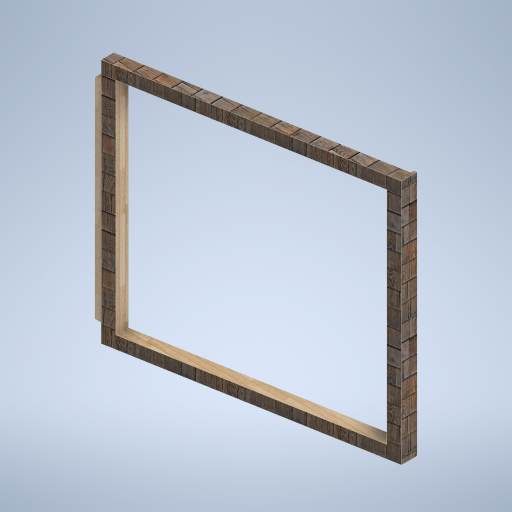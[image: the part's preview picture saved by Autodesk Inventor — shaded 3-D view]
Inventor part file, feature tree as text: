
AUTODESK INVENTOR PART (.ipt)
format: ipt  version: 2024.2 (Build 282272000, 272)  size: 413,184 bytes
history: native  units: mm
features: sketch x9, plane x4, extrude x4, loft x1, other x1, projected_geometry x1
ambient origin geometry x8: Origin, YZ Plane, XZ Plane, XY Plane, X Axis, Y Axis, Z Axis, Center Point
bodies: Solid1 (feature_tree)
feature tree (20):
  sketch  "Sketch1"  dims[d0=0.0mm d1=2500.0mm d2=150.0mm]
  plane  "Work Plane2"
  extrude  "Extrusion1"  Depth=150.0mm
  sketch  "Sketch2"  dims[d3=60.0mm d4=0.0mm d5=0.0mm]
  plane  "Work Plane3"
  sketch  "Sketch3"  dims[d6=13.962634mm d7=13.962634mm]
  plane  "Work Plane4"
  sketch  "Sketch4"  dims[d8=0.0mm d9=90.0deg d10=0.0mm d11=90.0deg]
  loft  "Loft1"
  extrude  "Extrusion2"  Depth=13.962634mm
  extrude  "Extrusion3"  TaperAngle=0.0deg  [1 undecoded]
  sketch  "Sketch8"  dims[d18=0.0mm d19=0.0mm]
  extrude  "Extrusion4"  Depth=2450.0mm
  plane  "Work Plane1"
  sketch  "Sketch5"  dims[d12=0.0mm d13=0.0mm d15=2450.0mm]
  other  "Edges1"
  sketch  "Sketch6"  dims[d16=30.0mm]
  sketch  "Sketch7"  dims[d17=2450.0mm]
  sketch  "Sketch9"  dims[d20=120.0mm d21=120.0mm d22=120.0mm d23=120.0mm d24=0.0mm d25=0.0mm]
  projected_geometry  "Projected Loop1"
note: 1 required parameter value undecoded (feature->parameter linkage not recoverable at this tier; creation-order binding heuristic only, values carry confidence <= 0.55)
